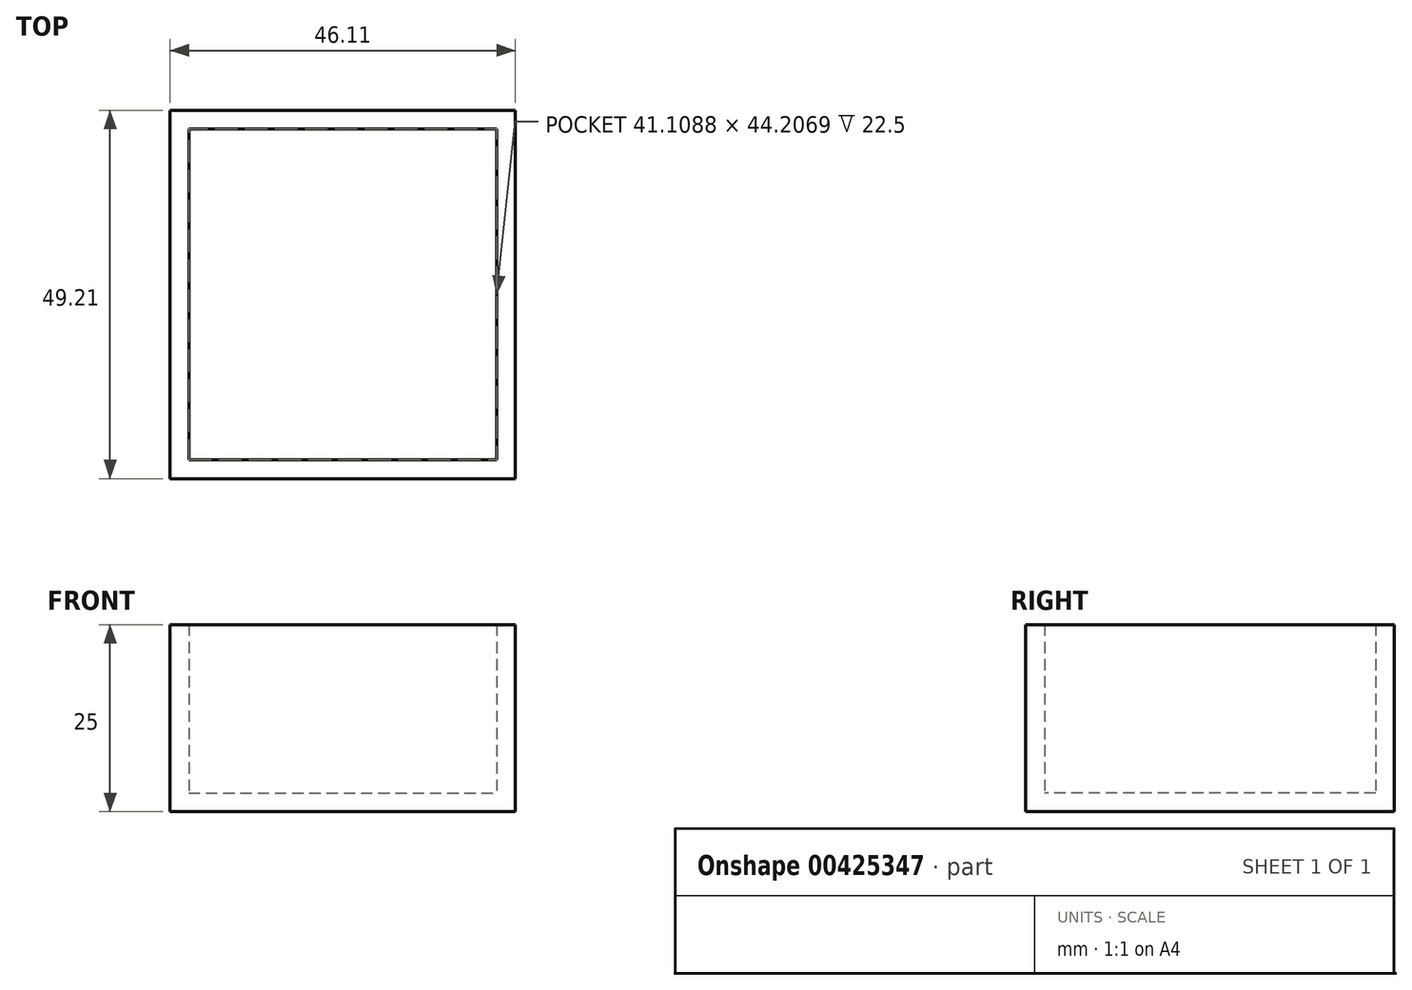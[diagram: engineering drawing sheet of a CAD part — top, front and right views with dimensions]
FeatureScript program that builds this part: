
annotation { "Feature Type Name" : "Feature", "Feature Type Description" : "" }
export const myFeature = defineFeature(function(context is Context, id is Id, definition is map)
    precondition{}
    {
        {
            var Q0;
            Q0=qCreatedBy(makeId("Top.planeOp"),FACE);
            var sketch = newSketch(context, id + "F0", { "sketchPlane" : qUnion([Q0])});
            skLineSegment(sketch, "E0.bottom", {"start": v(0, 0) * mm, "end": v(46.1, 0) * mm});
            skLineSegment(sketch, "E0.top", {"start": v(0, -49.2) * mm, "end": v(46.1, -49.2) * mm});
            skLineSegment(sketch, "E0.left", {"start": v(0, 0) * mm, "end": v(0, -49.2) * mm});
            skLineSegment(sketch, "E0.right", {"start": v(46.1, 0) * mm, "end": v(46.1, -49.2) * mm});
            skSolve(sketch);
        }
        {
            var Q0;
            Q0 = qSketchRegion(id + "F0", true);
            extrude(context, id + "F1", {"entities" : qUnion([Q0]), "depth" : 25 * mm, "offsetDistance" : 25 * mm});
        }
        {
            var Q0;
            Q0=makeQuery(id+"F1.opExtrude","CAP_FACE",FACE,{"disambiguationData":[OSD([sQuery(id+"F0.wireOp",EDGE,"E0.bottom"),sQuery(id+"F0.wireOp",EDGE,"E0.top"),sQuery(id+"F0.wireOp",EDGE,"E0.left"),sQuery(id+"F0.wireOp",EDGE,"E0.right")])],"isStart":false});
            shell(context, id + "F2", {"entities" : qUnion([Q0]), "thickness" : 2.5 * mm});
        }
    });
